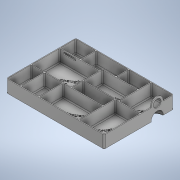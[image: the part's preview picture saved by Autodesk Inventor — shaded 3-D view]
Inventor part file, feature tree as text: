
AUTODESK INVENTOR PART (.ipt)
format: ipt  version: 2021 (Build 250183000, 183)  size: 3,420,160 bytes
history: native  units: mm
features: extrude x8, sketch x5, projected_geometry x4, fillet x1, chamfer x1
ambient origin geometry x8: Origin, YZ Plane, XZ Plane, XY Plane, X Axis, Y Axis, Z Axis, Center Point
bodies: Solid1 (feature_tree)
feature tree (19):
  sketch  "Sketch1"  dims[d0=200.0mm d1=142.25mm]
  extrude  "Extrusion1"  Depth=142.25mm
  extrude  "Extrusion2"  Depth=1.6mm
  extrude  "Extrusion4"  Depth=22.5mm
  extrude  "Extrusion5"  Depth=26.0mm
  extrude  "Extrusion6"  Depth=1.6mm
  sketch  "Sketch5"  dims[d6=46.0mm d7=26.0mm]
  extrude  "Extrusion7"  Depth=1.6mm
  extrude  "Extrusion8"  Depth=1.6mm
  extrude  "Extrusion9"  Depth=1.6mm
  fillet  "Fillet1"  Radius=1.6mm
  chamfer  "Chamfer1"  Distance=25.0mm
  sketch  "Sketch3"  dims[d2=1.6mm d3=43.0mm]
  projected_geometry  "Projected Loop2"
  sketch  "Sketch4"  dims[d4=65.0mm d5=22.5mm]
  projected_geometry  "Projected Loop3"
  projected_geometry  "Projected Loop4"
  sketch  "Sketch6"  dims[d8=48.0mm d9=1.6mm d11=1.6mm d12=1.6mm d17=1.6mm d18=1.6mm d19=25.0mm d20=0.0mm d21=1.0mm d22=0.0mm d23=28.5mm d24=39.0mm d26=40.0mm d27=41.0mm d28=45.0mm d29=56.85mm d30=55.1mm d31=79.0mm d32=80.0mm d36=32.5mm d37=44.5mm d38=36.0mm d39=72.45mm d40=62.4mm d41=48.0mm d42=50.0mm d43=1.6mm d44=1.6mm d45=61.0mm d46=30.0mm d47=22.85mm d48=21.5mm d49=55.0mm d50=2.181662mm d51=1.6mm d52=73.5mm d53=45.0mm d54=1.6mm d55=1.6mm d63=0.5mm d64=0.0mm d65=25.0mm d66=2.0mm d67=2.0mm d68=0.0mm d70=0.5mm d71=0.0mm d72=2.0mm d73=2.0mm d74=0.5mm d75=16.0mm d76=0.5mm d77=0.0mm d78=0.5mm d79=0.0mm d80=0.5mm d84=2.0mm d85=20.0mm d86=5.0mm d87=0.5mm d88=0.0mm d89=2.0mm d90=3.6mm d91=1.0mm d92=2.0mm d93=45.0deg d94=31.0mm d96=1.6mm d97=0.5mm d98=65.0mm d99=6.0mm]
  projected_geometry  "Projected Loop5"
